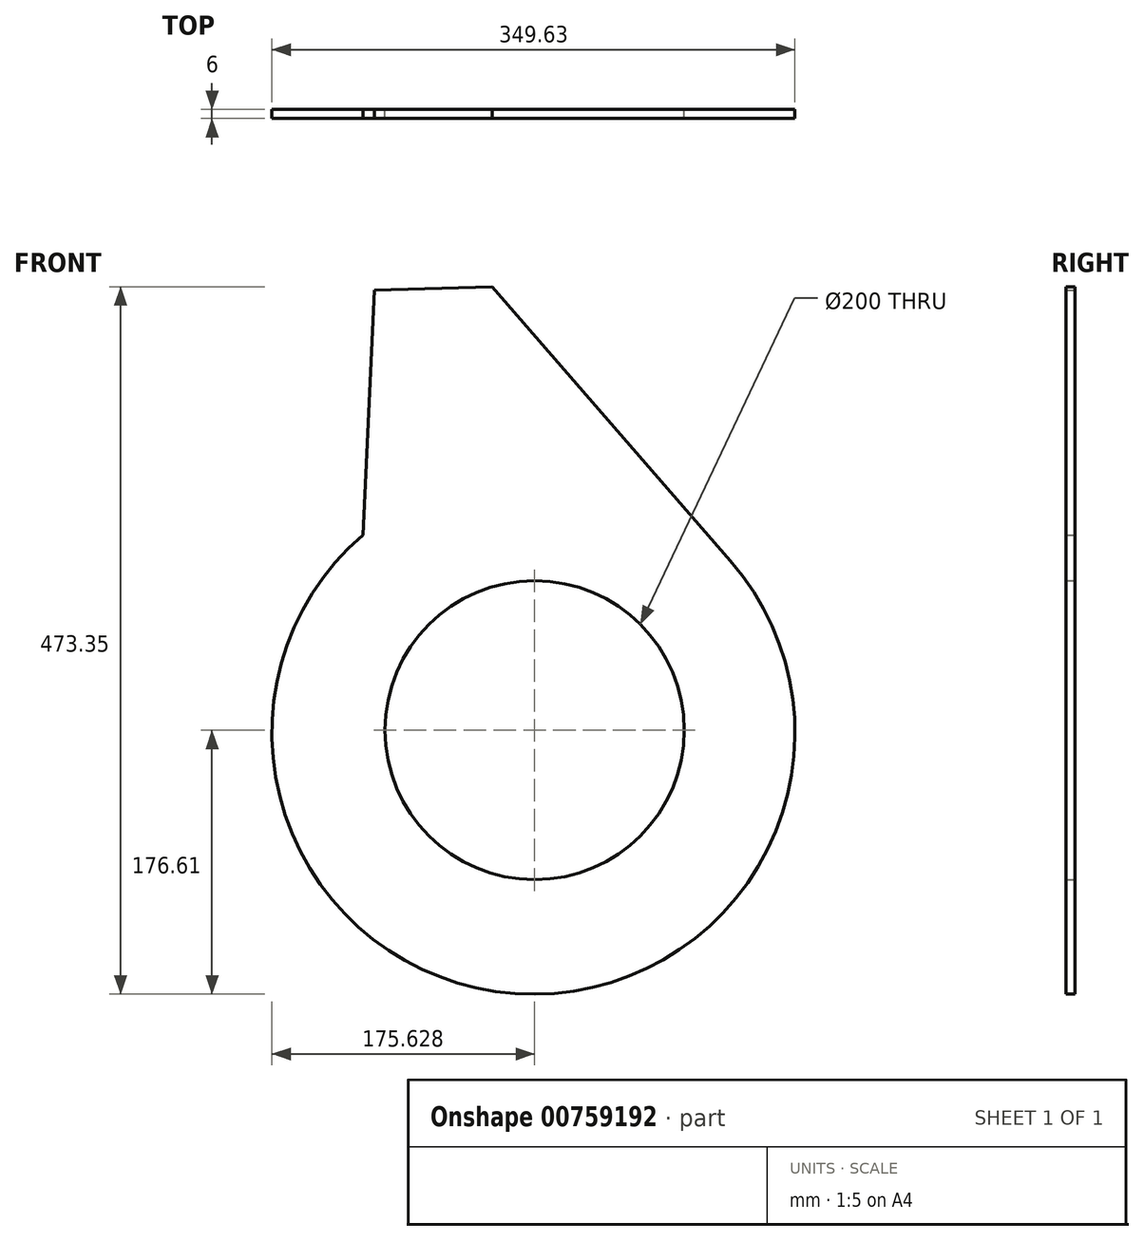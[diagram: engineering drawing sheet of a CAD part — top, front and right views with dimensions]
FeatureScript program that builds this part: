
annotation { "Feature Type Name" : "Feature", "Feature Type Description" : "" }
export const myFeature = defineFeature(function(context is Context, id is Id, definition is map)
    precondition{}
    {
        {
            var Q0;
            Q0=qCreatedBy(makeId("Front.planeOp"),FACE);
            var sketch = newSketch(context, id + "F0", { "sketchPlane" : qUnion([Q0])});
            skArc(sketch, "E0", {"start": v(43.16, -451.15) * mm, "mid": v(257.57, -420.58) * mm, "end": v(278.05, -204.96) * mm});
            skPoint(sketch, "E1.visualSharp", {"position": v(-26.65, -375.82) * mm});
            skPoint(sketch, "E2.visualSharp", {"position": v(-44, -296.33) * mm});
            skPoint(sketch, "E3.visualSharp", {"position": v(78.95, -135.37) * mm});
            skArc(sketch, "E4", {"start": v(16.9, -167.29) * mm, "mid": v(118.72, -474.16) * mm, "end": v(262.41, -184.53) * mm});
            skPoint(sketch, "E5.visualSharp", {"position": v(-32.6, -358.03) * mm});
            skPoint(sketch, "E6.visualSharp", {"position": v(-42.3, -280.12) * mm});
            skCircle(sketch, "E7", {"center": v(131.78, -297.98) * mm, "radius": 100 * mm});
            skPoint(sketch, "E8.visualSharp", {"position": v(70.14, -118.96) * mm});
            skLineSegment(sketch, "E9", {"start": v(16.9, -167.29) * mm, "end": v(24.72, -3.52) * mm});
            skLineSegment(sketch, "E10", {"start": v(103.28, -1.24) * mm, "end": v(263.52, -185.8) * mm});
            skLineSegment(sketch, "E11", {"start": v(24.72, -3.52) * mm, "end": v(103.28, -1.24) * mm});
            skSolve(sketch);
        }
        {
            var Q0;
            {var subQ0=sQuery(id+"F0.wireOp",EDGE,"E10");var subQ1=sQuery(id+"F0.wireOp",EDGE,"E4");var subQ2=makeQuery(id+"F0.imprint","INTERSECT",VERTEX,{"disambiguationData":[OD(0.0)],"derivedFrom":[subQ1,subQ0]});Q0=makeQuery(id+"F0.imprint","IMPRINT",FACE,{"disambiguationData":[TD([[makeQuery(id+"F0.imprint","IMPRINT",EDGE,{"disambiguationData":[TD([[subQ2,1.0]])],"derivedFrom":subQ1}),1.0]])]});}
            var Q1;
            Q1=makeQuery(id+"F0.imprint","IMPRINT",FACE,{"disambiguationData":[TD([[makeQuery(id+"F0.imprint","IMPRINT",EDGE,{"derivedFrom":sQuery(id+"F0.wireOp",EDGE,"E7")}),-1.0]])]});
            extrude(context, id + "F1", {"entities" : qUnion([Q0, Q1]), "depth" : 6 * mm, "offsetDistance" : 25 * mm});
        }
    });
